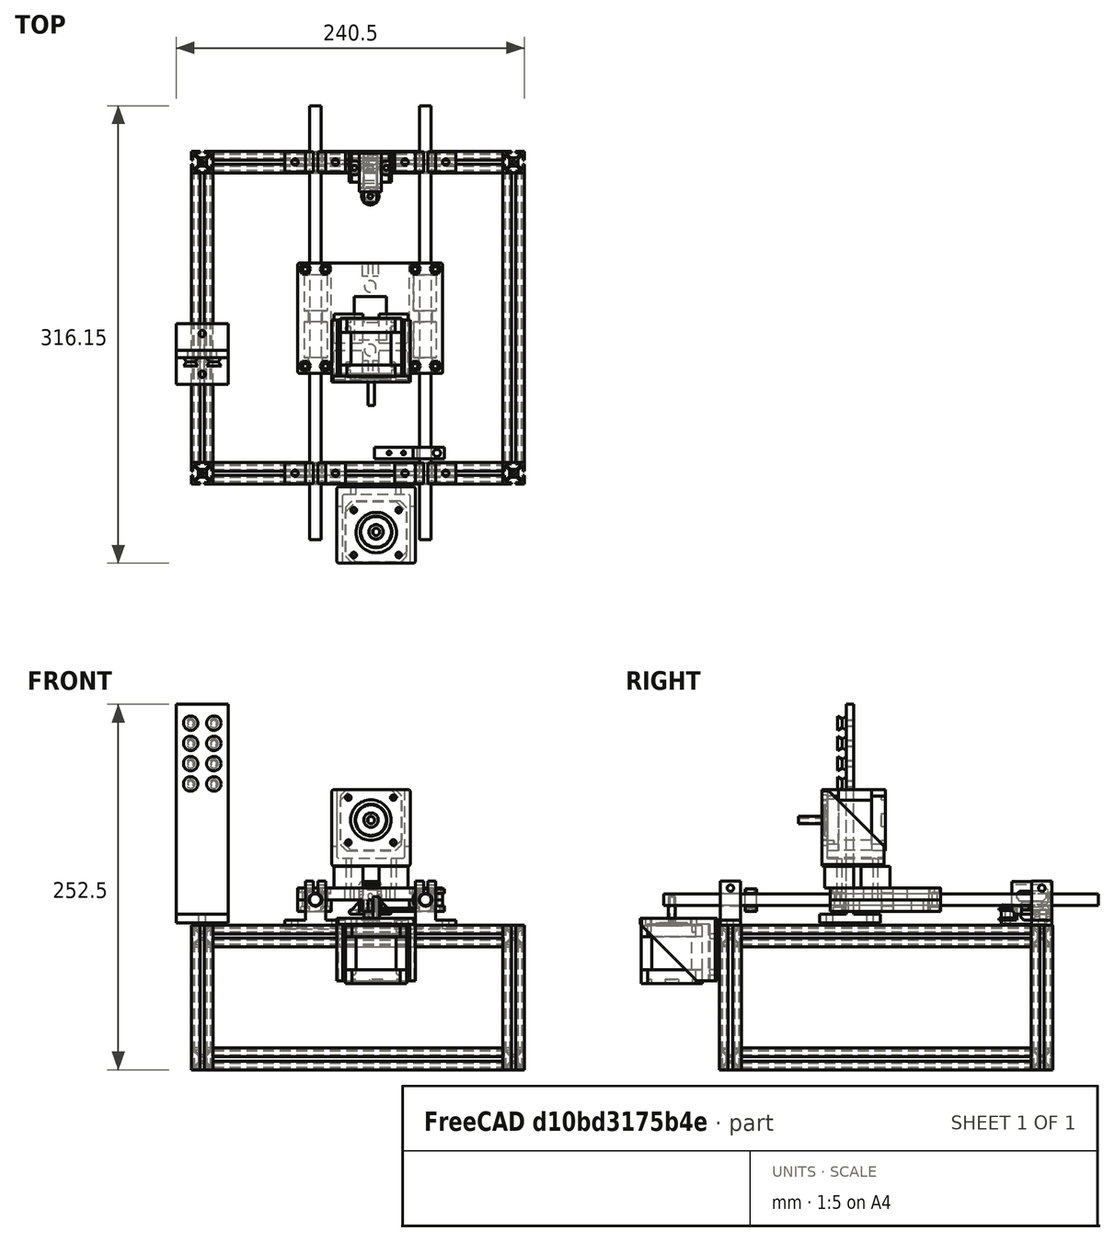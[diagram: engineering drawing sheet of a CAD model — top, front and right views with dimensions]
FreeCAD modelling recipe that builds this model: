
FCSTD DOCUMENT  (FreeCAD 0.16R6706 (Git))
Label: Coil winder
License: All rights reserved
LicenseURL: http://en.wikipedia.org/wiki/All_rights_reserved
objects: Part::Cut×44, Part::Cylinder×35, Part::Feature×20, Part::Box×7, Part::Prism×5, Part::Fillet×2, Part::Compound×1, Part::Fuse×1
note: 115 computed .brp shape members not serialized (recipe doc carries the construction recipe); baked Part::Feature solids carry a one-line shape summary decoded from their .brp

FEATURE [Part::Feature] aluprof_w15l_200
  Placement = pos=(7.5,1,0) rot=(0,0,1;0rad)
  shape: bbox 200 x 15 x 15 mm, 39 faces (baked)
FEATURE [Part::Feature] aluprof_w15l_201
  Placement = pos=(7.5,216,0) rot=(0,0,1;0rad)
  shape: bbox 200 x 15 x 15 mm, 39 faces (baked)
FEATURE [Part::Feature] aluprof_w15l_202
  Placement = pos=(0,8.5,0) rot=(0,0,1;1.5708rad)
  shape: bbox 15 x 200 x 15 mm, 39 faces (baked)
FEATURE [Part::Feature] aluprof_w15l_203
  Placement = pos=(215,8.5,0) rot=(0,0,1;1.5708rad)
  shape: bbox 15 x 200 x 15 mm, 39 faces (baked)
FEATURE [Part::Feature] aluprof_w15l_205
  Placement = pos=(7.5,1,85) rot=(0,0,1;0rad)
  shape: bbox 200 x 15 x 15 mm, 39 faces (baked)
FEATURE [Part::Feature] aluprof_w15l_206
  Placement = pos=(7.5,216,85) rot=(0,0,1;0rad)
  shape: bbox 200 x 15 x 15 mm, 39 faces (baked)
FEATURE [Part::Feature] aluprof_w15l_204
  Placement = pos=(215,8.5,85) rot=(0,0,1;1.5708rad)
  shape: bbox 15 x 200 x 15 mm, 39 faces (baked)
FEATURE [Part::Feature] aluprof_w15l_100
  Placement = pos=(0,1,92.5) rot=(0,1,0;1.5708rad)
  shape: bbox 15 x 15 x 100 mm, 39 faces (baked)
FEATURE [Part::Feature] aluprof_w15l_208
  Placement = pos=(0,216,92.5) rot=(0,1,0;1.5708rad)
  shape: bbox 15 x 15 x 100 mm, 39 faces (baked)
FEATURE [Part::Feature] aluprof_w15l_209
  Placement = pos=(215,216,92.5) rot=(0,1,0;1.5708rad)
  shape: bbox 15 x 15 x 100 mm, 39 faces (baked)
FEATURE [Part::Feature] aluprof_w15l_210
  Placement = pos=(215,1,92.5) rot=(0,1,0;1.5708rad)
  shape: bbox 15 x 15 x 100 mm, 39 faces (baked)
FEATURE [Part::Cylinder] Cylinder  label="Eje1"
  Angle = 360
  Height = 300
  Placement = pos=(154,255,110) rot=(1,0,0;1.5708rad)
  Radius = 4
FEATURE [Part::Cylinder] Cylinder001  label="Eje002"
  Angle = 360
  Height = 300
  Placement = pos=(78,255,110) rot=(1,0,0;1.5708rad)
  Radius = 4
FEATURE [Part::Feature] Fillet003001  label="Soporte principal "
  shape: bbox 100 x 76.1 x 16 mm, 90 faces (baked)
FEATURE [Part::Cylinder] Cylinder037  label="Cilindro022"
  Angle = 360
  Height = 20
  Placement = pos=(81,72,-10) rot=(0,0,1;0rad)
  Radius = 1.8
FEATURE [Part::Cut] Cut010035003015  label="Soporte principal'"
  Base = -> Fillet003001
  Tool = -> Cylinder037
FEATURE [Part::Prism] Prism004  label="Prisma004"
  Circumradius = 3.7
  Height = 10
  Placement = pos=(81,72,5) rot=(0,0,1;0rad)
  Polygon = 6
FEATURE [Part::Cut] Cut010035003016  label="Soporte principal''"
  Base = -> Cut010035003015
  Tool = -> Prism004
FEATURE [Part::Cylinder] Cylinder039  label="Cilindro024"
  Angle = 360
  Height = 20
  Placement = pos=(81,5,-10) rot=(0,0,1;0rad)
  Radius = 1.8
FEATURE [Part::Cut] Cut010035003019  label="Soporte principal ''''"
  Base = -> Cut010035003016
  Tool = -> Cylinder039
FEATURE [Part::Prism] Prism006  label="Prisma006"
  Circumradius = 3.7
  Height = 10
  Placement = pos=(81,5,4) rot=(0,0,1;0rad)
  Polygon = 6
FEATURE [Part::Cut] Cut010035003021  label="Soporte principal V"
  Base = -> Cut010035003019
  Tool = -> Prism006
FEATURE [Part::Cylinder] Cylinder043  label="Cilindro028"
  Angle = 360
  Height = 20
  Placement = pos=(19,72,-10) rot=(0,0,1;0rad)
  Radius = 1.8
FEATURE [Part::Cut] Cut010035003024  label="Soporte principal V'"
  Base = -> Cut010035003021
  Tool = -> Cylinder043
FEATURE [Part::Prism] Prism007  label="Prisma007"
  Circumradius = 3.7
  Height = 10
  Placement = pos=(19,72,5) rot=(0,0,1;0rad)
  Polygon = 6
FEATURE [Part::Cut] Cut010035003025  label="Soporte principal V'''"
  Base = -> Cut010035003024
  Tool = -> Prism007
FEATURE [Part::Cylinder] Cylinder046  label="Cilindro031"
  Angle = 360
  Height = 20
  Placement = pos=(19,5,-10) rot=(0,0,1;0rad)
  Radius = 1.8
FEATURE [Part::Cut] Cut010035003028  label="Soporte principal VI"
  Base = -> Cut010035003025
  Tool = -> Cylinder046
FEATURE [Part::Prism] Prism008  label="Prisma008"
  Circumradius = 3.7
  Height = 10
  Placement = pos=(19,5,4) rot=(0,0,1;0rad)
  Polygon = 6
FEATURE [Part::Cut] Cut010035003029  label="Soporte principal VI'"
  Base = -> Cut010035003028
  Tool = -> Prism008
FEATURE [Part::Cylinder] Cylinder047
  Angle = 360
  Height = 100
  Placement = pos=(12,79,0) rot=(1,0,0;1.5708rad)
  Radius = 4.7
FEATURE [Part::Cylinder] Cylinder048
  Angle = 360
  Height = 100
  Placement = pos=(88,79,0) rot=(1,0,0;1.5708rad)
  Radius = 4.7
FEATURE [Part::Cut] Cut
  Base = -> Cut010035003029
  Tool = -> Cylinder047
FEATURE [Part::Cut] Cut010035003030  label="Soporte principal VII"
  Base = -> Cut
  Placement = pos=(66,70,110) rot=(0,0,1;0rad)
  Tool = -> Cylinder048
FEATURE [Part::Cylinder] Cylinder049
  Angle = 360
  Height = 100
  Placement = pos=(12,79,0) rot=(1,0,0;1.5708rad)
  Radius = 4.7
FEATURE [Part::Cylinder] Cylinder050
  Angle = 360
  Height = 100
  Placement = pos=(88,79,0) rot=(1,0,0;1.5708rad)
  Radius = 4.7
FEATURE [Part::Box] Box011  label="Cubo007"
  Height = 8
  Length = 23
  Placement = pos=(0,0,-8) rot=(0,0,1;0rad)
  Width = 76.1
FEATURE [Part::Cylinder] Cylinder028  label="Rodamiento 009"
  Angle = 360
  Height = 24.85
  Placement = pos=(12.25,35.55,0) rot=(1,0,0;1.5708rad)
  Radius = 7.8
FEATURE [Part::Cylinder] Cylinder029  label="Rodamiento 010"
  Angle = 360
  Height = 24.85
  Placement = pos=(12.25,68.1,0) rot=(1,0,0;1.5708rad)
  Radius = 7.8
FEATURE [Part::Cylinder] Cylinder030  label="Eje 005"
  Angle = 360
  Height = 76.1
  Placement = pos=(12.25,76.1,0) rot=(1,0,0;1.5708rad)
  Radius = 4.4
FEATURE [Part::Cut] Cut010035003006
  Base = -> Box011
  Tool = -> Cylinder028
FEATURE [Part::Cut] Cut010035003007
  Base = -> Cut010035003006
  Tool = -> Cylinder030
FEATURE [Part::Cut] Cut010035003008
  Base = -> Cut010035003007
  Tool = -> Cylinder029
FEATURE [Part::Cylinder] Cylinder031  label="Cilindro016"
  Angle = 360
  Height = 20
  Placement = pos=(5,5,-10) rot=(0,0,1;0rad)
  Radius = 1.8
FEATURE [Part::Cylinder] Cylinder032  label="Cilindro017"
  Angle = 360
  Height = 20
  Placement = pos=(5,72,-10) rot=(0,0,1;0rad)
  Radius = 1.8
FEATURE [Part::Cut] Cut010035003009
  Base = -> Cut010035003008
  Tool = -> Cylinder032
FEATURE [Part::Cut] Cut010035003010
  Base = -> Cut010035003009
  Tool = -> Cylinder031
FEATURE [Part::Fillet] Fillet003002  label="Carcasa 005"
  Base = -> Cut010035003010
  Edges = 4 edges r=1: [Edge1,Edge3,Edge5,Edge22]
FEATURE [Part::Cylinder] Cylinder033  label="Cilindro018"
  Angle = 360
  Height = 10
  Placement = pos=(5,5,-15) rot=(0,0,1;0rad)
  Radius = 3
FEATURE [Part::Cylinder] Cylinder034  label="Cilindro019"
  Angle = 360
  Height = 10
  Placement = pos=(5,72,-15) rot=(0,0,1;0rad)
  Radius = 3
FEATURE [Part::Cut] Cut010035003011
  Base = -> Fillet003002
  Tool = -> Cylinder033
FEATURE [Part::Cut] Cut010035003012  label="Carcasa 2'"
  Base = -> Cut010035003011
  Tool = -> Cylinder034
FEATURE [Part::Feature] Fusion002001  label="Fusion004"
  shape: bbox 23 x 76.1 x 8 mm, 26 faces (baked)
FEATURE [Part::Fillet] Fillet003003  label="Carcasa 1'"
  Base = -> Fusion002001
  Edges = 2 edges r=1: [Edge61,Edge63]
FEATURE [Part::Cylinder] Cylinder035  label="Cilindro020"
  Angle = 360
  Height = 10
  Placement = pos=(81,72,-15) rot=(0,0,1;0rad)
  Radius = 3
FEATURE [Part::Cylinder] Cylinder036  label="Cilindro021"
  Angle = 360
  Height = 20
  Placement = pos=(81,72,-10) rot=(0,0,1;0rad)
  Radius = 1.8
FEATURE [Part::Cut] Cut010035003013
  Base = -> Fillet003003
  Tool = -> Cylinder035
FEATURE [Part::Cut] Cut010035003014  label="Carcasa 1''"
  Base = -> Cut010035003013
  Tool = -> Cylinder036
FEATURE [Part::Prism] Prism005  label="Prisma005"
  Circumradius = 3.7
  Height = 10
  Placement = pos=(81,5,5) rot=(0,0,1;0rad)
  Polygon = 6
FEATURE [Part::Cylinder] Cylinder038  label="Cilindro023"
  Angle = 360
  Height = 20
  Placement = pos=(81,5,-10) rot=(0,0,1;0rad)
  Radius = 1.8
FEATURE [Part::Cut] Cut010035003017
  Base = -> Cut010035003014
  Tool = -> Prism005
FEATURE [Part::Cut] Cut010035003018  label="Carcasa 1'''"
  Base = -> Cut010035003017
  Tool = -> Cylinder038
FEATURE [Part::Cylinder] Cylinder040  label="Cilindro025"
  Angle = 360
  Height = 10
  Placement = pos=(81,5,-15) rot=(0,0,1;0rad)
  Radius = 3
FEATURE [Part::Cut] Cut010035003020  label="Carcasa 1 V"
  Base = -> Cut010035003018
  Tool = -> Cylinder040
FEATURE [Part::Cylinder] Cylinder041  label="Cilindro026"
  Angle = 360
  Height = 10
  Placement = pos=(19,72,-15) rot=(0,0,1;0rad)
  Radius = 3
FEATURE [Part::Cylinder] Cylinder042  label="Cilindro027"
  Angle = 360
  Height = 20
  Placement = pos=(19,72,-10) rot=(0,0,1;0rad)
  Radius = 1.8
FEATURE [Part::Cut] Cut010035003022
  Base = -> Cut010035003012
  Tool = -> Cylinder041
FEATURE [Part::Cut] Cut010035003023  label="Carcasa 2 '''"
  Base = -> Cut010035003022
  Tool = -> Cylinder042
FEATURE [Part::Cylinder] Cylinder044  label="Cilindro029"
  Angle = 360
  Height = 10
  Placement = pos=(19,5,-15) rot=(0,0,1;0rad)
  Radius = 3
FEATURE [Part::Cylinder] Cylinder045  label="Cilindro030"
  Angle = 360
  Height = 20
  Placement = pos=(19,5,-10) rot=(0,0,1;0rad)
  Radius = 1.8
FEATURE [Part::Cut] Cut010035003026
  Base = -> Cut010035003023
  Tool = -> Cylinder044
FEATURE [Part::Cut] Cut010035003027  label="Carcasa 2 V"
  Base = -> Cut010035003026
  Tool = -> Cylinder045
FEATURE [Part::Cut] Cut010035003031  label="Carcasa 1 VI"
  Base = -> Cut010035003020
  Placement = pos=(66,70,110) rot=(0,0,1;0rad)
  Tool = -> Cylinder050
FEATURE [Part::Cut] Cut010035003032  label="Carcasa 2 VI"
  Base = -> Cut010035003027
  Placement = pos=(66,70,110) rot=(0,0,1;0rad)
  Tool = -> Cylinder049
FEATURE [Part::Cylinder] Cylinder008  label="Cilindro002"
  Angle = 360
  Height = 40
  Placement = pos=(34.5,31,-11) rot=(0,0,1;0rad)
  Radius = 1.8
FEATURE [Part::Cylinder] Cylinder009  label="Cilindro003"
  Angle = 360
  Height = 40
  Placement = pos=(65.5,31,-11) rot=(0,0,1;0rad)
  Radius = 1.8
FEATURE [Part::Cylinder] Cylinder006  label="Cilindro"
  Angle = 360
  Height = 40
  Placement = pos=(34.5,6,-11) rot=(0,0,1;0rad)
  Radius = 1.8
FEATURE [Part::Cylinder] Cylinder007  label="Cilindro001"
  Angle = 360
  Height = 40
  Placement = pos=(65.5,6,-11) rot=(0,0,1;0rad)
  Radius = 1.8
FEATURE [Part::Feature] nema_holder
  Placement = pos=(49.9,39,-32) rot=(0.57735,0.57735,-0.57735;2.0944rad)
  shape: bbox 54.3 x 43 x 52.8 mm, 27 faces (baked)
FEATURE [Part::Cut] Cut010035003002
  Base = -> nema_holder
  Tool = -> Cylinder006
FEATURE [Part::Cut] Cut010035003003
  Base = -> Cut010035003002
  Tool = -> Cylinder007
FEATURE [Part::Cut] Cut010035003004
  Base = -> Cut010035003003
  Tool = -> Cylinder009
FEATURE [Part::Cut] Cut010035003005  label="nema holder modificados taladros"
  Base = -> Cut010035003004
  Placement = pos=(66.5,107,133) rot=(1,0,0;3.14159rad)
  Tool = -> Cylinder008
FEATURE [Part::Cylinder] Cylinder017  label="Taladro tornillo010"
  Angle = 360
  Height = 80
  Placement = pos=(-20,10,10) rot=(0,1,0;1.5708rad)
  Radius = 1.7
FEATURE [Part::Box] Box  label="Cubo"
  Height = 20
  Length = 15
  Width = 20
FEATURE [Part::Cut] Cut010035003033
  Base = -> Box
  Placement = pos=(91,66,133) rot=(0,1,0;1.5708rad)
  Tool = -> Cylinder017
FEATURE [Part::Cylinder] Cylinder051  label="Taladro tornillo011"
  Angle = 360
  Height = 80
  Placement = pos=(-20,10,10) rot=(0,1,0;1.5708rad)
  Radius = 1.7
FEATURE [Part::Box] Box012  label="Cubo008"
  Height = 20
  Length = 15
  Width = 20
FEATURE [Part::Cut] Cut010035003034
  Base = -> Box012
  Placement = pos=(122,66,133) rot=(0,1,0;1.5708rad)
  Tool = -> Cylinder051
FEATURE [Part::Cylinder] Cylinder052  label="Taladro tornillo012"
  Angle = 360
  Height = 80
  Placement = pos=(-20,10,10) rot=(0,1,0;1.5708rad)
  Radius = 1.7
FEATURE [Part::Box] Box013  label="Cubo009"
  Height = 20
  Length = 15
  Width = 20
FEATURE [Part::Cut] Cut010035003035
  Base = -> Box013
  Placement = pos=(122,91,133) rot=(0,1,0;1.5708rad)
  Tool = -> Cylinder052
FEATURE [Part::Cylinder] Cylinder053  label="Taladro tornillo013"
  Angle = 360
  Height = 80
  Placement = pos=(-20,10,10) rot=(0,1,0;1.5708rad)
  Radius = 1.7
FEATURE [Part::Box] Box014  label="Cubo010"
  Height = 20
  Length = 15
  Width = 20
FEATURE [Part::Cut] Cut010035003036
  Base = -> Box014
  Placement = pos=(91,91,133) rot=(0,1,0;1.5708rad)
  Tool = -> Cylinder053
FEATURE [Part::Feature] Chamfer001  label="Nema-17-motor-40mm-final"
  Placement = pos=(116.5,108,165) rot=(1,0,0;1.5708rad)
  shape: bbox 42.3 x 60.1 x 42.3 mm, 55 faces (baked)
FEATURE [Part::Cylinder] Cylinder054  label="Cilindro032"
  Angle = 360
  Height = 30
  Placement = pos=(21.158,20,20) rot=(1,0,0;1.5708rad)
  Radius = 4.5
FEATURE [Part::Feature] Cut003001001  label="Cut005"
  shape: bbox 42 x 14 x 33 mm, 13 faces (baked)
FEATURE [Part::Cut] Cut003001002
  Base = -> Cut003001001
  Tool = -> Cylinder054
FEATURE [Part::Box] Box002  label="Cubo002"
  Height = 30
  Length = 3
  Placement = pos=(19.73,0,20) rot=(0,0,1;0rad)
  Width = 30
FEATURE [Part::Cut] Cut003001003  label="Soporte eje"
  Base = -> Cut003001002
  Placement = pos=(57,-6,90) rot=(0,0,1;0rad)
  Tool = -> Box002
FEATURE [Part::Cylinder] Cylinder055  label="Cilindro033"
  Angle = 360
  Height = 30
  Placement = pos=(21.158,20,20) rot=(1,0,0;1.5708rad)
  Radius = 4.5
FEATURE [Part::Feature] Cut010035003037  label="Cut010035003043"
  shape: bbox 42 x 14 x 33 mm, 13 faces (baked)
FEATURE [Part::Cut] Cut010035003038
  Base = -> Cut010035003037
  Tool = -> Cylinder055
FEATURE [Part::Box] Box015  label="Cubo011"
  Height = 30
  Length = 3
  Placement = pos=(19.73,0,20) rot=(0,0,1;0rad)
  Width = 30
FEATURE [Part::Cut] Cut010035003039  label="Soporte eje001"
  Base = -> Cut010035003038
  Placement = pos=(133,-6,90) rot=(0,0,1;0rad)
  Tool = -> Box015
FEATURE [Part::Cut] Cut010035003040  label="Soporte eje002"
  Base = -> Cut010035003038
  Placement = pos=(133,209,90) rot=(0,0,1;0rad)
  Tool = -> Box015
FEATURE [Part::Cut] Cut010035003041  label="Soporte eje003"
  Base = -> Cut003001002
  Placement = pos=(57,209,90) rot=(0,0,1;0rad)
  Tool = -> Box002
FEATURE [Part::Feature] tensioner_holder
  Placement = pos=(116,222,100) rot=(0,0,-1;1.5708rad)
  shape: bbox 29 x 26.6 x 22.5 mm, 55 faces (baked)
FEATURE [Part::Compound] idler_tensioner_set
  Placement = pos=(116,222,100) rot=(0,0,-1;1.5708rad)
FEATURE [Part::Cut] Cut010035003042  label="nema holder modificados taladros001"
  Base = -> Cut010035003004
  Placement = pos=(170,-8,54) rot=(0,0.707107,0.707107;3.14159rad)
  Tool = -> Cylinder008
FEATURE [Part::Feature] Chamfer002  label="Nema-17-motor-40mm-final001"
  Placement = pos=(120,-39.5,52) rot=(0,0,1;0rad)
  shape: bbox 42.3 x 42.3 x 60.1 mm, 55 faces (baked)
FEATURE [Part::Cut] Cut007  label="Soporte finalcarrera"
  Placement = pos=(158,19,102) rot=(0,0,1;3.14159rad)
FEATURE [Part::Feature] aluprof_w15l_207
  Placement = pos=(0,8.5,85) rot=(0,0,1;1.5708rad)
  shape: bbox 15 x 200 x 15 mm, 39 faces (baked)
FEATURE [Part::Fuse] Fusion001002017008
  Placement = pos=(-18,81,100) rot=(0,0,1;4.71239rad)
